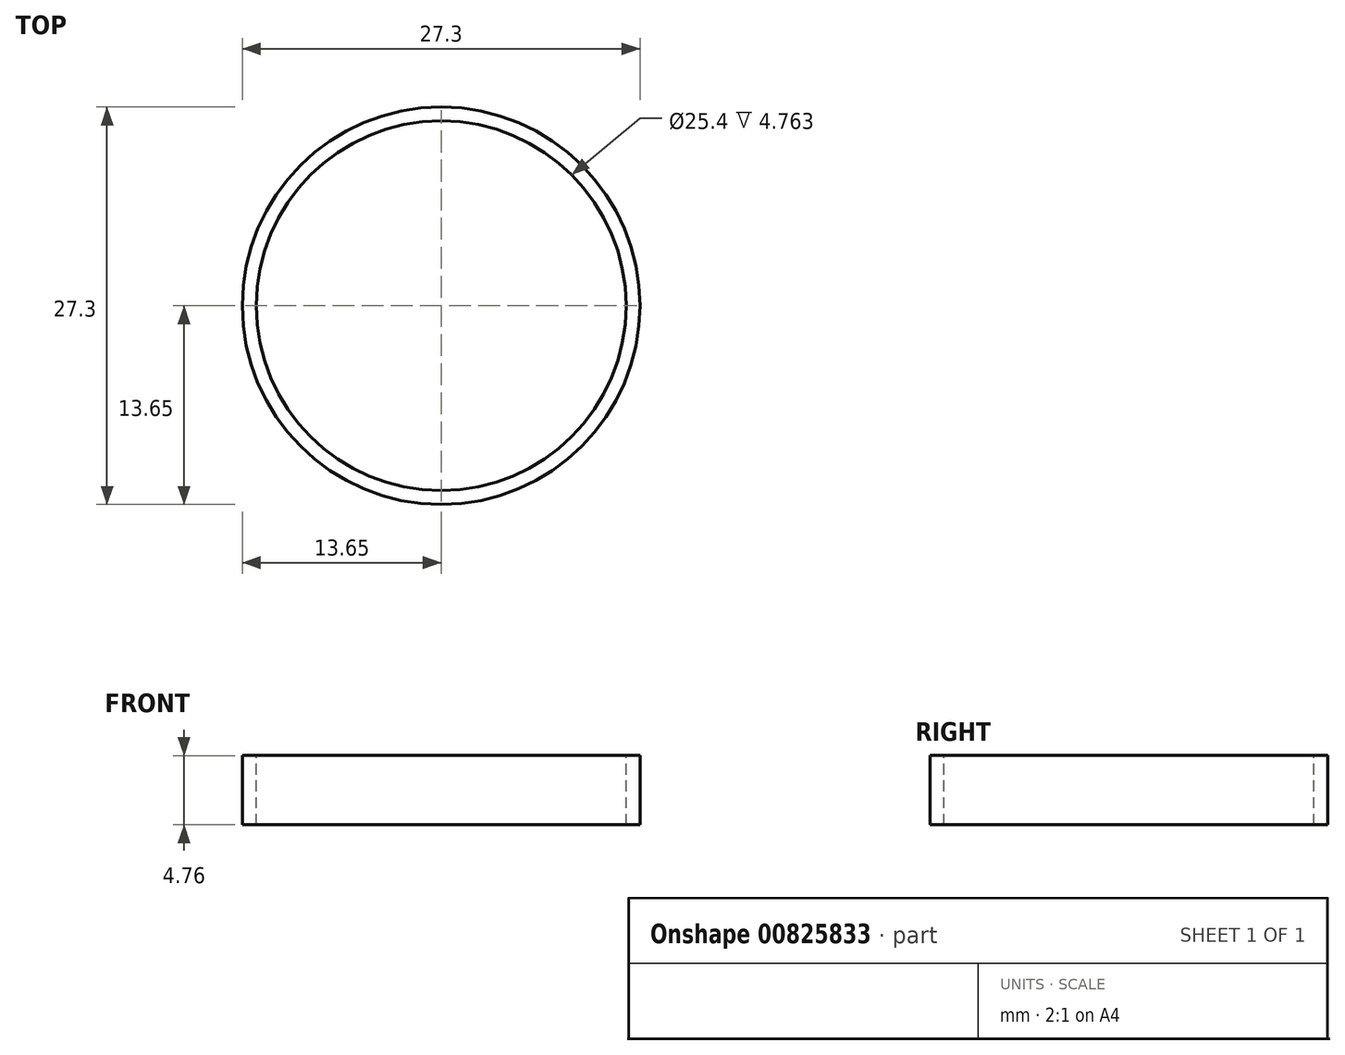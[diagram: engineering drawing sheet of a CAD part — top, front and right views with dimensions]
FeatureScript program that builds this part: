
annotation { "Feature Type Name" : "Feature", "Feature Type Description" : "" }
export const myFeature = defineFeature(function(context is Context, id is Id, definition is map)
    precondition{}
    {
        {
            var Q0;
            Q0=qCreatedBy(makeId("Front.planeOp"),FACE);
            var sketch = newSketch(context, id + "F0", { "sketchPlane" : qUnion([Q0])});
            skLineSegment(sketch, "E0", {"start": v(0, 2.38) * mm, "end": v(0, -2.38) * mm, "construction": true});
            skLineSegment(sketch, "E1.bottom", {"start": v(-12.7, 2.38) * mm, "end": v(-13.65, 2.38) * mm});
            skLineSegment(sketch, "E1.top", {"start": v(-12.7, -2.38) * mm, "end": v(-13.65, -2.38) * mm});
            skLineSegment(sketch, "E1.left", {"start": v(-12.7, 2.38) * mm, "end": v(-12.7, -2.38) * mm});
            skLineSegment(sketch, "E1.right", {"start": v(-13.65, 2.38) * mm, "end": v(-13.65, -2.38) * mm});
            skPoint(sketch, "E2", {"position": v(0, 0) * mm});
            skSolve(sketch);
        }
        {
            var Q0;
            Q0=makeQuery(id+"F0.imprint","IMPRINT",FACE,{"disambiguationData":[TD([[makeQuery(id+"F0.imprint","IMPRINT",EDGE,{"derivedFrom":sQuery(id+"F0.wireOp",EDGE,"E1.bottom")}),1.0]])]});
            var Q1;
            Q1=sQuery(id+"F0.wireOp",EDGE,"E0");
            revolve(context, id + "F1", {"surfaceOperationType" : NewSurfaceOperationType.NEW, "entities" : qUnion([Q0]), "axis" : qUnion([Q1]), "revolveType" : RevolveType.FULL});
        }
    });
